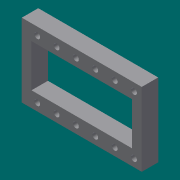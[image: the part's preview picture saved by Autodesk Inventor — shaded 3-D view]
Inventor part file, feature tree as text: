
AUTODESK INVENTOR PART (.ipt)
format: ipt  version: 2013 (Build 170138000, 138)  size: 97,280 bytes
history: native  units: mm
features: extrude x2, sketch x2, other x1
ambient origin geometry x8: Origin, YZ Plane, XZ Plane, XY Plane, X Axis, Y Axis, Z Axis, Center Point
feature tree (5):
  other  "ソリッド1"
  extrude  "押し出し1"  Depth=8.5mm TaperAngle=0.0deg
  extrude  "押し出し2"  Depth=5.0mm
  sketch  "スケッチ1"
  sketch  "スケッチ2"
